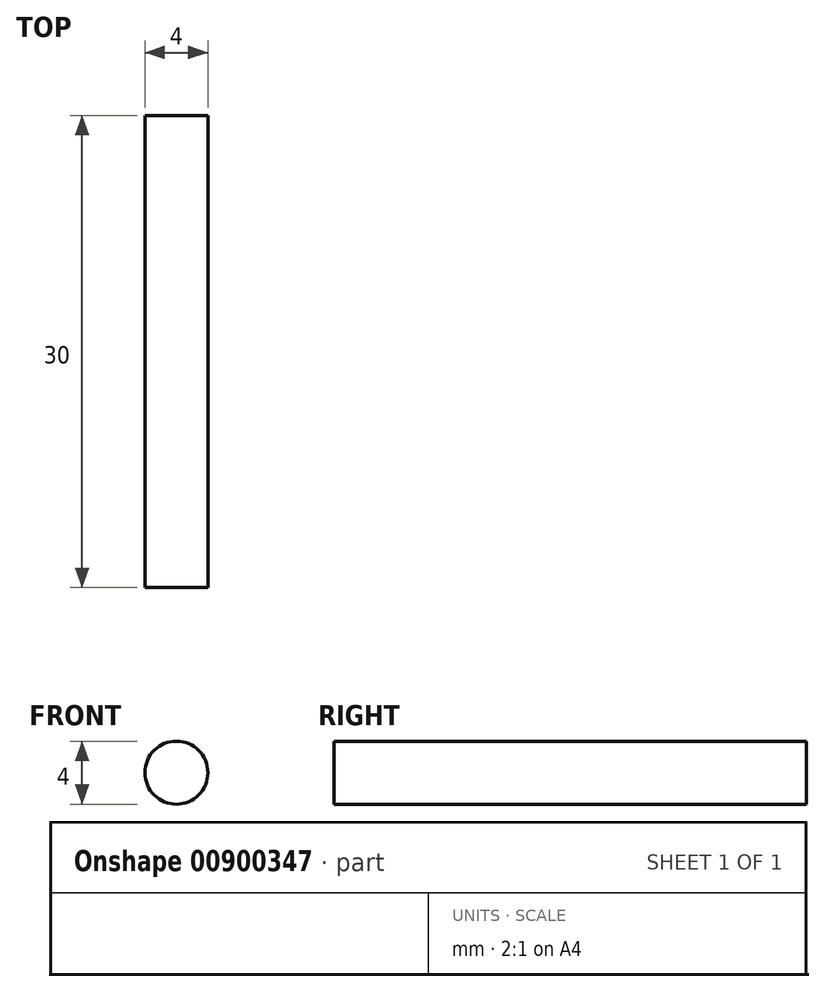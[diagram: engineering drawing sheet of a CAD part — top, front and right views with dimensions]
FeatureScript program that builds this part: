
annotation { "Feature Type Name" : "Feature", "Feature Type Description" : "" }
export const myFeature = defineFeature(function(context is Context, id is Id, definition is map)
    precondition{}
    {
        {
            var Q0;
            Q0=qCreatedBy(makeId("Front.planeOp"),FACE);
            var sketch = newSketch(context, id + "F0", { "sketchPlane" : qUnion([Q0])});
            skCircle(sketch, "E0", {"center": v(0, 0) * mm, "radius": 2 * mm});
            skSolve(sketch);
        }
        {
            var Q0;
            Q0=makeQuery(id+"F0.imprint","IMPRINT",FACE,{"disambiguationData":[TD([[makeQuery(id+"F0.imprint","IMPRINT",EDGE,{"derivedFrom":sQuery(id+"F0.wireOp",EDGE,"E0")}),1.0]])]});
            extrude(context, id + "F1", {"entities" : qUnion([Q0]), "depth" : 30 * mm, "offsetDistance" : 25.4 * mm});
        }
    });
